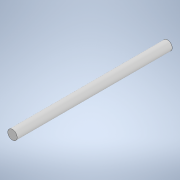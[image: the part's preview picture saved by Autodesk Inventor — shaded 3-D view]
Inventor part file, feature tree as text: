
AUTODESK INVENTOR PART (.ipt)
format: ipt  version: 2021 (Build 250183000, 183)  size: 92,160 bytes
history: native  units: mm
features: extrude x1, sketch x1
ambient origin geometry x8: Origin, YZ Plane, XZ Plane, XY Plane, X Axis, Y Axis, Z Axis, Center Point
bodies: Solid1 (feature_tree)
feature tree (2):
  extrude  "Extrusion1"  Depth=49.5mm TaperAngle=0.0deg
  sketch  "Sketch1"  dims[d0=3.0mm d1=49.5mm d2=0.0mm d3=0.5mm d4=0.872665mm d5=0.5mm d6=0.872665mm]
